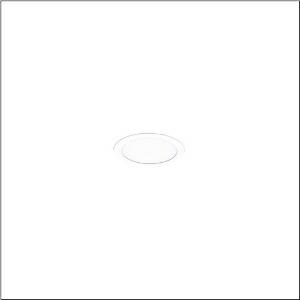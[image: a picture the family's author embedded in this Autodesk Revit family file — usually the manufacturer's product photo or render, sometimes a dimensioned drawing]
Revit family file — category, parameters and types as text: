
# Revit family: lunis_21_s_51db16ma91c
name_source: partatom
category: Lighting Fixtures
units: mm (PartAtom-declared; Revit-internal decimal feet)

## family parameters
Cut with Voids When Loaded = No
Host = Face
Light Source = No
Part Type = Normal
Room Calculation Point = No
Round Connector Dimension = Use Diameter
Shared = No

## types (1)
- --- (1 x LED, 790 lm, 5.9 W, 6500K)
    Apparent Load = 6 VA
    CIE Flux Codes = 50 80 96 100 100
    Color Rendering = 80
    Color Temperature = 6500K
    Default Elevation = 1800 mm
    Description = Lunis 21,  S, downlight, light control with lens, of PMMA, optical cover: cover panel, of PC, opal, light emission: direct distribution, LED rated luminous flux: 800lm, light colour: 830/840/865, with terminal, 3-pole, mains connection: 220..240V, AC, 50..60Hz, housing, round, of diecast aluminium, traffic white (RAL 9016), diameter: 84mm, clamping range: 1..40mm, protection rating (complete): IP20, protection rating (on room side): IP54, insulation class (complete): insulation class II (safety insulation), certification: CE, impact resistance: IK03, packaging unit: 1 piece
    Height = 0 mm  [stored 0 ft]
    Lamp = 1 x LED
    Lamp Light Flux = 790 lm
    Lamp Power = 5.9 W
    Lamp count = 1
    Length = 84 mm
    Luminous efficacy = 134 lm/W
    Manufacturer = Siteco
    ModVariant = No
    Model = 51DB16MA91C
    Mounting Place = Ceiling
    Mounting Type = Recessed
    Number of Poles = 1
    OnlyDefault = Yes
    Power Factor = 1
    Product Name = Lunis 21 S
    Product group = downlight
    ProductGroupID = 400
    Protection Class = Protection class II
    Protection Degree = IP 20
    RLX_Detail_Level = 1
    RLX_Emergency_Light_Flux = 0 lm
    RLX_Emergency_Type = 0
    RLX_Emergency_Type_DB = No
    RlxData = <blob elided: 7693 chars, md5=837b1380>
    Socket = socket
    Standby Power = 0 W
    System Light Flux = 790 lm
    System Power = 6 W
    Type Comments = individual setting: colour temperature 6500K
    Type Image = l_1290838.jpg
    URL = http://relux.com
    VarID = @adj_021060
    Voltage = 0 V
    Weight = 0.00 kg
    Width = 0 mm  [stored 0 ft]

note: [stored X ft] marks values corroborated as IEEE doubles in the binary element streams (Revit-internal decimal feet)

## geometry (parser evidence)
native form markers: Sweep x9
no freeform markers — native parametric forms only
